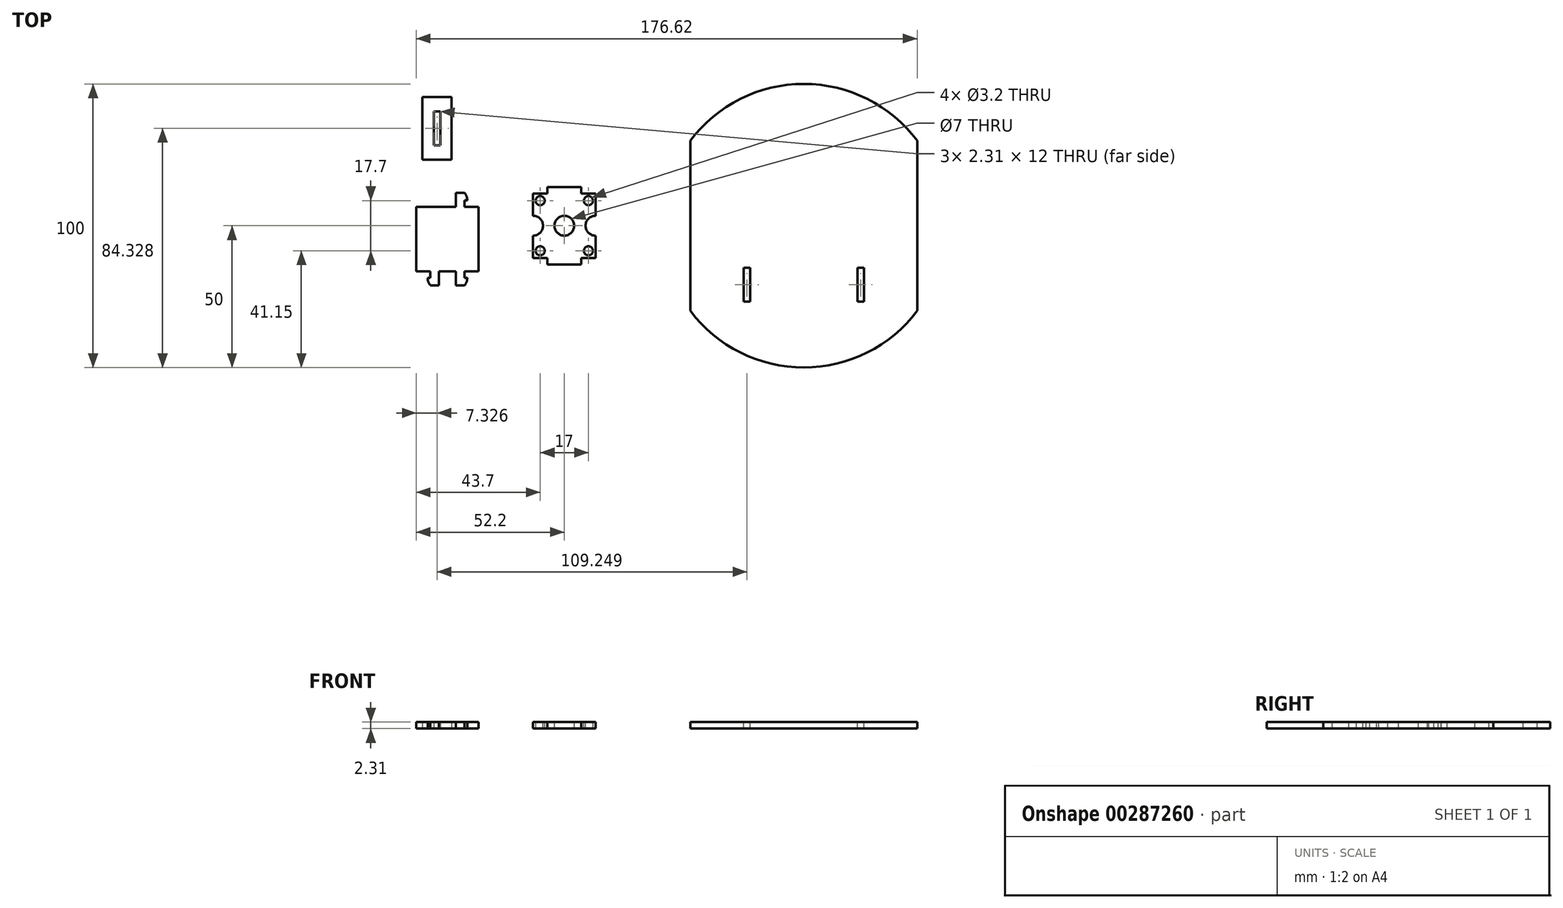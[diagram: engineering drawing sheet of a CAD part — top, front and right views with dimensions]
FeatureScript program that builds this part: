
annotation { "Feature Type Name" : "Feature", "Feature Type Description" : "" }
export const myFeature = defineFeature(function(context is Context, id is Id, definition is map)
    precondition{}
    {
        {
            var Q0;
            Q0=qCreatedBy(makeId("Top.planeOp"),FACE);
            var sketch = newSketch(context, id + "F0", { "sketchPlane" : qUnion([Q0])});
            skLineSegment(sketch, "E0.bottom", {"start": v(11, -11.35) * mm, "end": v(-11, -11.35) * mm});
            skLineSegment(sketch, "E0.top", {"start": v(11, 11.35) * mm, "end": v(-11, 11.35) * mm});
            skLineSegment(sketch, "E0.left", {"start": v(11, -11.35) * mm, "end": v(11, 11.35) * mm});
            skLineSegment(sketch, "E0.right", {"start": v(-11, -11.35) * mm, "end": v(-11, 11.35) * mm});
            skPoint(sketch, "E0.middle", {"position": v(0, 0) * mm});
            skSolve(sketch);
        }
        {
            var Q0;
            Q0=makeQuery(id+"F0.imprint","IMPRINT",FACE,{"disambiguationData":[TD([[makeQuery(id+"F0.imprint","IMPRINT",EDGE,{"derivedFrom":sQuery(id+"F0.wireOp",EDGE,"E0.bottom")}),-1.0]])]});
            extrude(context, id + "F1", {"entities" : qUnion([Q0]), "depth" : 2.31 * mm});
        }
        {
            var Q0;
            Q0=makeQuery(id+"F1.opExtrude","CAP_FACE",FACE,{"disambiguationData":[OSD([sQuery(id+"F0.wireOp",EDGE,"E0.bottom"),sQuery(id+"F0.wireOp",EDGE,"E0.top"),sQuery(id+"F0.wireOp",EDGE,"E0.left"),sQuery(id+"F0.wireOp",EDGE,"E0.right")])],"isStart":false});
            var sketch = newSketch(context, id + "F2", { "sketchPlane" : qUnion([Q0])});
            skPoint(sketch, "E1", {"position": v(-8.5, 8.85) * mm});
            skPoint(sketch, "E2.MirrorP", {"position": v(-8.5, -8.85) * mm});
            skPoint(sketch, "E3.MirrorP", {"position": v(8.5, 8.85) * mm});
            skPoint(sketch, "E4.MirrorP", {"position": v(8.5, -8.85) * mm});
            skSolve(sketch);
        }
        {
            var Q0;
            Q0=sQuery(id+"F2.wireOp",VERTEX,"E1");
            var Q1;
            Q1=sQuery(id+"F2.wireOp",VERTEX,"E3.MirrorP");
            var Q2;
            Q2=sQuery(id+"F2.wireOp",VERTEX,"E4.MirrorP");
            var Q3;
            Q3=sQuery(id+"F2.wireOp",VERTEX,"E2.MirrorP");
            var Q4;
            Q4=makeQuery(id+"F1.opExtrude","SWEPT_BODY",BODY,{"disambiguationData":[OSD([sQuery(id+"F0.wireOp",EDGE,"E0.bottom"),sQuery(id+"F0.wireOp",EDGE,"E0.top"),sQuery(id+"F0.wireOp",EDGE,"E0.left"),sQuery(id+"F0.wireOp",EDGE,"E0.right")])]});
            hole(context, id + "F3", {"style" : HoleStyle.SIMPLE, "endStyle" : HoleEndStyle.THROUGH, "holeDiameter" : 3.2 * mm, "tappedDepth" : 12 * mm, "tapClearance" : 3, "locations" : qUnion([Q0, Q1, Q2, Q3]), "scope" : qUnion([Q4])});
        }
        {
            var Q0;
            Q0=makeQuery(id+"F1.opExtrude","CAP_FACE",FACE,{"disambiguationData":[OSD([sQuery(id+"F0.wireOp",EDGE,"E0.bottom"),sQuery(id+"F0.wireOp",EDGE,"E0.top"),sQuery(id+"F0.wireOp",EDGE,"E0.left"),sQuery(id+"F0.wireOp",EDGE,"E0.right")])],"isStart":false});
            var sketch = newSketch(context, id + "F4", { "sketchPlane" : qUnion([Q0])});
            skLineSegment(sketch, "E5.bottom", {"start": v(6, -13.66) * mm, "end": v(-6, -13.66) * mm});
            skLineSegment(sketch, "E5.top", {"start": v(6, 13.66) * mm, "end": v(-6, 13.66) * mm});
            skLineSegment(sketch, "E5.left", {"start": v(6, -13.66) * mm, "end": v(6, 13.66) * mm});
            skLineSegment(sketch, "E5.right", {"start": v(-6, -13.66) * mm, "end": v(-6, 13.66) * mm});
            skPoint(sketch, "E5.middle", {"position": v(0, 0) * mm});
            skSolve(sketch);
        }
        {
            var Q0;
            {var subQ0=sQuery(id+"F4.wireOp",EDGE,"E5.top");Q0=makeQuery(id+"F4.imprint","IMPRINT",FACE,{"disambiguationData":[TD([[makeQuery(id+"F4.imprint","IMPRINT",EDGE,{"derivedFrom":subQ0}),1.0]])]});}
            var Q1;
            {var subQ0=sQuery(id+"F4.wireOp",EDGE,"E5.bottom");Q1=makeQuery(id+"F4.imprint","IMPRINT",FACE,{"disambiguationData":[TD([[makeQuery(id+"F4.imprint","IMPRINT",EDGE,{"derivedFrom":subQ0}),-1.0]])]});}
            extrude(context, id + "F5", {"entities" : qUnion([Q0, Q1]), "oppositeDirection" : true, "depth" : 2.31 * mm});
        }
        {
            var Q0;
            Q0=makeQuery(id+"F1.opExtrude","SWEPT_BODY",BODY,{"disambiguationData":[OSD([sQuery(id+"F0.wireOp",EDGE,"E0.bottom"),sQuery(id+"F0.wireOp",EDGE,"E0.top"),sQuery(id+"F0.wireOp",EDGE,"E0.left"),sQuery(id+"F0.wireOp",EDGE,"E0.right")])]});
            var Q1;
            Q1=makeQuery(id+"F5.opExtrude","SWEPT_BODY",BODY,{"disambiguationData":[OSD([sQuery(id+"F0.wireOp",EDGE,"E0.top"),sQuery(id+"F4.wireOp",EDGE,"E5.top"),sQuery(id+"F4.wireOp",EDGE,"E5.left"),sQuery(id+"F4.wireOp",EDGE,"E5.right")])]});
            var Q2;
            Q2=makeQuery(id+"F5.opExtrude","SWEPT_BODY",BODY,{"disambiguationData":[OSD([sQuery(id+"F0.wireOp",EDGE,"E0.bottom"),sQuery(id+"F4.wireOp",EDGE,"E5.bottom"),sQuery(id+"F4.wireOp",EDGE,"E5.left"),sQuery(id+"F4.wireOp",EDGE,"E5.right")])]});
            booleanBodies(context, id + "F6", {"operationType" : BooleanOperationType.UNION, "tools" : qUnion([Q0, Q1, Q2])});
        }
        {
            var Q0;
            {var subQ0=sQuery(id+"F4.wireOp",EDGE,"E5.right");var subQ1=sQuery(id+"F4.wireOp",EDGE,"E5.left");var subQ2=sQuery(id+"F0.wireOp",EDGE,"E0.top");var subQ3=sQuery(id+"F0.wireOp",EDGE,"E0.bottom");Q0=makeQuery(id+"F6.opBoolean","MERGE",FACE,{"derivedFrom":[makeQuery(id+"F1.opExtrude","CAP_FACE",FACE,{"disambiguationData":[OSD([subQ3,subQ2,sQuery(id+"F0.wireOp",EDGE,"E0.left"),sQuery(id+"F0.wireOp",EDGE,"E0.right")])],"isStart":false}),makeQuery(id+"F5.opExtrude","CAP_FACE",FACE,{"disambiguationData":[OSD([subQ3,sQuery(id+"F4.wireOp",EDGE,"E5.bottom"),subQ1,subQ0])],"isStart":true}),makeQuery(id+"F5.opExtrude","CAP_FACE",FACE,{"disambiguationData":[OSD([subQ2,sQuery(id+"F4.wireOp",EDGE,"E5.top"),subQ1,subQ0])],"isStart":true})]});}
            var sketch = newSketch(context, id + "F7", { "sketchPlane" : qUnion([Q0])});
            skPoint(sketch, "E6", {"position": v(-11, 0) * mm});
            skPoint(sketch, "E7", {"position": v(11, 0) * mm});
            skPoint(sketch, "E8", {"position": v(0, 0) * mm});
            skSolve(sketch);
        }
        {
            var Q0;
            Q0=sQuery(id+"F7.wireOp",VERTEX,"E6");
            var Q1;
            Q1=sQuery(id+"F7.wireOp",VERTEX,"E7");
            var Q2;
            Q2=sQuery(id+"F7.wireOp",VERTEX,"E8");
            var Q3;
            Q3=makeQuery(id+"F1.opExtrude","SWEPT_BODY",BODY,{"disambiguationData":[OSD([sQuery(id+"F0.wireOp",EDGE,"E0.bottom"),sQuery(id+"F0.wireOp",EDGE,"E0.top"),sQuery(id+"F0.wireOp",EDGE,"E0.left"),sQuery(id+"F0.wireOp",EDGE,"E0.right")])]});
            hole(context, id + "F8", {"style" : HoleStyle.SIMPLE, "endStyle" : HoleEndStyle.THROUGH, "holeDiameter" : 7 * mm, "tappedDepth" : 12 * mm, "tapClearance" : 3, "locations" : qUnion([Q0, Q1, Q2]), "scope" : qUnion([Q3])});
        }
        {
            var Q0;
            Q0=qCreatedBy(makeId("Top.planeOp"),FACE);
            var sketch = newSketch(context, id + "F9", { "sketchPlane" : qUnion([Q0])});
            skCircle(sketch, "E9", {"center": v(84.42, 0) * mm, "radius": 50 * mm});
            skLineSegment(sketch, "E10.bottom", {"start": v(44.42, 50) * mm, "end": v(124.42, 50) * mm});
            skLineSegment(sketch, "E10.top", {"start": v(44.42, -50) * mm, "end": v(124.42, -50) * mm});
            skLineSegment(sketch, "E10.left", {"start": v(44.42, 50) * mm, "end": v(44.42, -50) * mm});
            skLineSegment(sketch, "E10.right", {"start": v(124.42, 50) * mm, "end": v(124.42, -50) * mm});
            skLineSegment(sketch, "E11", {"start": v(84.42, 50) * mm, "end": v(84.42, 0) * mm});
            skPoint(sketch, "E12", {"position": v(84.42, 50) * mm});
            skSolve(sketch);
        }
        {
            var Q0;
            Q0=makeQuery(id+"F9.imprint","IMPRINT",FACE,{"disambiguationData":[TD([[makeQuery(id+"F9.imprint","IMPRINT",EDGE,{"derivedFrom":sQuery(id+"F9.wireOp",EDGE,"n7RTJ1XV-eWxd-Xe3c-fP3V-9vTSdCg1LdaS.bottom")}),-1.0]])]});
            var Q1;
            {var subQ0=sQuery(id+"F9.wireOp",EDGE,"E9");var subQ7=makeQuery(id+"F9.imprint","INTERSECT",VERTEX,{"derivedFrom":[subQ0,sQuery(id+"F9.wireOp",EDGE,"E10.bottom")]});Q1=makeQuery(id+"F9.imprint","IMPRINT",FACE,{"disambiguationData":[TD([[makeQuery(id+"F9.imprint","IMPRINT",EDGE,{"disambiguationData":[TD([[subQ7,1.0]])],"derivedFrom":subQ0}),1.0]])]});}
            extrude(context, id + "F10", {"entities" : qUnion([Q0, Q1]), "depth" : 2.31 * mm});
        }
        {
            var Q0;
            Q0=makeQuery(id+"F10.opExtrude","CAP_FACE",FACE,{"disambiguationData":[OSD([sQuery(id+"F9.wireOp",EDGE,"E9"),sQuery(id+"F9.wireOp",EDGE,"E10.left"),sQuery(id+"F9.wireOp",EDGE,"E10.right")])],"isStart":false});
            var sketch = newSketch(context, id + "F11", { "sketchPlane" : qUnion([Q0])});
            skLineSegment(sketch, "E13.bottom", {"start": v(63.22, -14.83) * mm, "end": v(65.53, -14.83) * mm});
            skLineSegment(sketch, "E13.top", {"start": v(63.22, -26.83) * mm, "end": v(65.53, -26.83) * mm});
            skLineSegment(sketch, "E13.left", {"start": v(63.22, -14.83) * mm, "end": v(63.22, -26.83) * mm});
            skLineSegment(sketch, "E13.right", {"start": v(65.53, -14.83) * mm, "end": v(65.53, -26.83) * mm});
            skLineSegment(sketch, "E14", {"start": v(84.42, 50) * mm, "end": v(84.42, -50) * mm});
            skLineSegment(sketch, "E15.MirrorCS", {"start": v(105.62, -14.83) * mm, "end": v(103.3, -14.83) * mm});
            skLineSegment(sketch, "E16.MirrorCS", {"start": v(105.62, -26.83) * mm, "end": v(103.3, -26.83) * mm});
            skLineSegment(sketch, "E17.MirrorCS", {"start": v(103.3, -14.83) * mm, "end": v(103.3, -26.83) * mm});
            skLineSegment(sketch, "E18.MirrorCS", {"start": v(105.62, -14.83) * mm, "end": v(105.62, -26.83) * mm});
            skSolve(sketch);
        }
        {
            var Q0;
            Q0=makeQuery(id+"F11.imprint","IMPRINT",FACE,{"disambiguationData":[TD([[makeQuery(id+"F11.imprint","IMPRINT",EDGE,{"derivedFrom":sQuery(id+"F11.wireOp",EDGE,"E13.bottom")}),-1.0]])]});
            var Q1;
            Q1=makeQuery(id+"F11.imprint","IMPRINT",FACE,{"disambiguationData":[TD([[makeQuery(id+"F11.imprint","IMPRINT",EDGE,{"derivedFrom":sQuery(id+"F11.wireOp",EDGE,"E15.MirrorCS")}),1.0]])]});
            extrude(context, id + "F12", {"entities" : qUnion([Q0, Q1]), "operationType" : NewBodyOperationType.REMOVE, "endBound" : BoundingType.THROUGH_ALL, "oppositeDirection" : true, "depth" : 2.2 * mm});
        }
        {
            var Q0;
            Q0=qCreatedBy(makeId("Top.planeOp"),FACE);
            var sketch = newSketch(context, id + "F13", { "sketchPlane" : qUnion([Q0])});
            skLineSegment(sketch, "E19.bottom", {"start": v(-52.2, 6.6) * mm, "end": v(-30.2, 6.6) * mm});
            skLineSegment(sketch, "E19.top", {"start": v(-52.2, -16.1) * mm, "end": v(-30.2, -16.1) * mm});
            skLineSegment(sketch, "E19.left", {"start": v(-52.2, 6.6) * mm, "end": v(-52.2, -16.1) * mm});
            skLineSegment(sketch, "E19.right", {"start": v(-30.2, 6.6) * mm, "end": v(-30.2, -16.1) * mm});
            skLineSegment(sketch, "E20", {"start": v(-41.2, -16.1) * mm, "end": v(-41.2, 6.6) * mm});
            skLineSegment(sketch, "E21", {"start": v(-47.2, 8.91) * mm, "end": v(-47.2, -4.75) * mm});
            skLineSegment(sketch, "E22", {"start": v(-44.2, 8.91) * mm, "end": v(-44.2, -4.75) * mm});
            skCircle(sketch, "E23", {"center": v(-42.22, 33.17) * mm, "radius": 4 * mm});
            skLineSegment(sketch, "E24", {"start": v(-42.22, 33.17) * mm, "end": v(-42.22, 37.17) * mm});
            skLineSegment(sketch, "E25", {"start": v(-42.22, 33.17) * mm, "end": v(-46.22, 33.17) * mm});
            skArc(sketch, "E26", {"start": v(-48.2, 8.91) * mm, "mid": v(-47.94, 10.33) * mm, "end": v(-47.2, 11.56) * mm});
            skLineSegment(sketch, "E27", {"start": v(-47.2, 8.91) * mm, "end": v(-48.2, 8.91) * mm});
            skLineSegment(sketch, "E28", {"start": v(-47.2, 11.56) * mm, "end": v(-44.2, 11.56) * mm});
            skLineSegment(sketch, "E29", {"start": v(-44.2, 11.56) * mm, "end": v(-44.2, 8.91) * mm});
            skLineSegment(sketch, "E30", {"start": v(-52.2, -4.75) * mm, "end": v(-30.2, -4.75) * mm});
            skLineSegment(sketch, "E31.MirrorCS", {"start": v(-47.2, -18.41) * mm, "end": v(-48.2, -18.41) * mm});
            skLineSegment(sketch, "E32.MirrorCS", {"start": v(-44.2, -21.06) * mm, "end": v(-44.2, -18.41) * mm});
            skLineSegment(sketch, "E33.MirrorCS", {"start": v(-47.2, -18.41) * mm, "end": v(-47.2, -4.75) * mm});
            skLineSegment(sketch, "E34.MirrorCS", {"start": v(-44.2, -18.41) * mm, "end": v(-44.2, -4.75) * mm});
            skLineSegment(sketch, "E35.MirrorCS", {"start": v(-47.2, -21.06) * mm, "end": v(-44.2, -21.06) * mm});
            skArc(sketch, "E36.MirrorCS", {"start": v(-48.2, -18.41) * mm, "mid": v(-47.94, -19.83) * mm, "end": v(-47.2, -21.06) * mm});
            skLineSegment(sketch, "E37.MirrorCS", {"start": v(-35.2, 8.91) * mm, "end": v(-34.2, 8.91) * mm});
            skLineSegment(sketch, "E38.MirrorCS", {"start": v(-35.2, -18.41) * mm, "end": v(-34.2, -18.41) * mm});
            skLineSegment(sketch, "E39.MirrorCS", {"start": v(-35.2, 8.91) * mm, "end": v(-35.2, -4.75) * mm});
            skArc(sketch, "E40.MirrorCS", {"start": v(-34.2, -18.41) * mm, "mid": v(-34.46, -19.83) * mm, "end": v(-35.2, -21.06) * mm});
            skLineSegment(sketch, "E41.MirrorCS", {"start": v(-35.2, -18.41) * mm, "end": v(-35.2, -4.75) * mm});
            skLineSegment(sketch, "E42.MirrorCS", {"start": v(-38.2, 8.91) * mm, "end": v(-38.2, -4.75) * mm});
            skLineSegment(sketch, "E43.MirrorCS", {"start": v(-38.2, -21.06) * mm, "end": v(-38.2, -18.41) * mm});
            skLineSegment(sketch, "E44.MirrorCS", {"start": v(-35.2, 11.56) * mm, "end": v(-38.2, 11.56) * mm});
            skArc(sketch, "E45.MirrorCS", {"start": v(-34.2, 8.91) * mm, "mid": v(-34.46, 10.33) * mm, "end": v(-35.2, 11.56) * mm});
            skLineSegment(sketch, "E46.MirrorCS", {"start": v(-38.2, 11.56) * mm, "end": v(-38.2, 8.91) * mm});
            skLineSegment(sketch, "E47.MirrorCS", {"start": v(-38.2, -18.41) * mm, "end": v(-38.2, -4.75) * mm});
            skLineSegment(sketch, "E48.MirrorCS", {"start": v(-35.2, -21.06) * mm, "end": v(-38.2, -21.06) * mm});
            skSolve(sketch);
        }
        {
            var Q0;
            {var subQ0=sQuery(id+"F13.wireOp",EDGE,"E19.left");var subQ1=sQuery(id+"F13.wireOp",EDGE,"E19.bottom");var subQ2=makeQuery(id+"F13.imprint","INTERSECT",VERTEX,{"derivedFrom":[subQ1,subQ0]});Q0=makeQuery(id+"F13.imprint","IMPRINT",FACE,{"disambiguationData":[TD([[makeQuery(id+"F13.imprint","IMPRINT",EDGE,{"disambiguationData":[TD([[subQ2,-1.0]])],"derivedFrom":subQ1}),-1.0]])]});}
            var Q1;
            {var subQ0=sQuery(id+"F13.wireOp",EDGE,"E21");var subQ1=sQuery(id+"F13.wireOp",EDGE,"E19.bottom");var subQ2=makeQuery(id+"F13.imprint","INTERSECT",VERTEX,{"derivedFrom":[subQ1,subQ0]});Q1=makeQuery(id+"F13.imprint","IMPRINT",FACE,{"disambiguationData":[TD([[makeQuery(id+"F13.imprint","IMPRINT",EDGE,{"disambiguationData":[TD([[subQ2,-1.0]])],"derivedFrom":subQ1}),-1.0]])]});}
            var Q2;
            {var subQ0=sQuery(id+"F13.wireOp",EDGE,"E20");var subQ1=sQuery(id+"F13.wireOp",EDGE,"E19.bottom");var subQ2=makeQuery(id+"F13.imprint","INTERSECT",VERTEX,{"derivedFrom":[subQ1,subQ0]});Q2=makeQuery(id+"F13.imprint","IMPRINT",FACE,{"disambiguationData":[TD([[makeQuery(id+"F13.imprint","IMPRINT",EDGE,{"disambiguationData":[TD([[subQ2,-1.0]])],"derivedFrom":subQ1}),-1.0]])]});}
            var Q3;
            {var subQ0=sQuery(id+"F13.wireOp",EDGE,"E20");var subQ1=sQuery(id+"F13.wireOp",EDGE,"E19.top");var subQ2=makeQuery(id+"F13.imprint","INTERSECT",VERTEX,{"derivedFrom":[subQ1,subQ0]});Q3=makeQuery(id+"F13.imprint","IMPRINT",FACE,{"disambiguationData":[TD([[makeQuery(id+"F13.imprint","IMPRINT",EDGE,{"disambiguationData":[TD([[subQ2,-1.0]])],"derivedFrom":subQ1}),1.0]])]});}
            var Q4;
            {var subQ0=sQuery(id+"F13.wireOp",EDGE,"E19.left");var subQ1=sQuery(id+"F13.wireOp",EDGE,"E19.top");var subQ2=makeQuery(id+"F13.imprint","INTERSECT",VERTEX,{"derivedFrom":[subQ1,subQ0]});Q4=makeQuery(id+"F13.imprint","IMPRINT",FACE,{"disambiguationData":[TD([[makeQuery(id+"F13.imprint","IMPRINT",EDGE,{"disambiguationData":[TD([[subQ2,-1.0]])],"derivedFrom":subQ1}),1.0]])]});}
            var Q5;
            {var subQ0=sQuery(id+"F13.wireOp",EDGE,"E19.right");var subQ1=sQuery(id+"F13.wireOp",EDGE,"E19.top");var subQ2=makeQuery(id+"F13.imprint","INTERSECT",VERTEX,{"derivedFrom":[subQ1,subQ0]});Q5=makeQuery(id+"F13.imprint","IMPRINT",FACE,{"disambiguationData":[TD([[makeQuery(id+"F13.imprint","IMPRINT",EDGE,{"disambiguationData":[TD([[subQ2,1.0]])],"derivedFrom":subQ1}),1.0]])]});}
            var Q6;
            {var subQ0=sQuery(id+"F13.wireOp",EDGE,"E19.right");var subQ1=sQuery(id+"F13.wireOp",EDGE,"E19.bottom");var subQ2=makeQuery(id+"F13.imprint","INTERSECT",VERTEX,{"derivedFrom":[subQ1,subQ0]});Q6=makeQuery(id+"F13.imprint","IMPRINT",FACE,{"disambiguationData":[TD([[makeQuery(id+"F13.imprint","IMPRINT",EDGE,{"disambiguationData":[TD([[subQ2,1.0]])],"derivedFrom":subQ1}),-1.0]])]});}
            var Q7;
            {var subQ1=sQuery(id+"F13.wireOp",EDGE,"E38.MirrorCS");Q7=makeQuery(id+"F13.imprint","IMPRINT",FACE,{"disambiguationData":[TD([[makeQuery(id+"F13.imprint","IMPRINT",EDGE,{"derivedFrom":subQ1}),-1.0]])]});}
            var Q8;
            {var subQ0=sQuery(id+"F13.wireOp",EDGE,"E33.MirrorCS");var subQ1=sQuery(id+"F13.wireOp",EDGE,"E19.top");var subQ2=makeQuery(id+"F13.imprint","INTERSECT",VERTEX,{"derivedFrom":[subQ1,subQ0]});Q8=makeQuery(id+"F13.imprint","IMPRINT",FACE,{"disambiguationData":[TD([[makeQuery(id+"F13.imprint","IMPRINT",EDGE,{"disambiguationData":[TD([[subQ2,-1.0]])],"derivedFrom":subQ1}),1.0]])]});}
            var Q9;
            {var subQ0=sQuery(id+"F13.wireOp",EDGE,"E42.MirrorCS");var subQ1=sQuery(id+"F13.wireOp",EDGE,"E19.bottom");var subQ2=makeQuery(id+"F13.imprint","INTERSECT",VERTEX,{"derivedFrom":[subQ1,subQ0]});Q9=makeQuery(id+"F13.imprint","IMPRINT",FACE,{"disambiguationData":[TD([[makeQuery(id+"F13.imprint","IMPRINT",EDGE,{"disambiguationData":[TD([[subQ2,-1.0]])],"derivedFrom":subQ1}),-1.0]])]});}
            var Q10;
            {var subQ0=sQuery(id+"F13.wireOp",EDGE,"E20");var subQ1=sQuery(id+"F13.wireOp",EDGE,"E19.bottom");var subQ2=makeQuery(id+"F13.imprint","INTERSECT",VERTEX,{"derivedFrom":[subQ1,subQ0]});Q10=makeQuery(id+"F13.imprint","IMPRINT",FACE,{"disambiguationData":[TD([[makeQuery(id+"F13.imprint","IMPRINT",EDGE,{"disambiguationData":[TD([[subQ2,1.0]])],"derivedFrom":subQ1}),-1.0]])]});}
            var Q11;
            {var subQ0=sQuery(id+"F13.wireOp",EDGE,"E20");var subQ1=sQuery(id+"F13.wireOp",EDGE,"E19.top");var subQ2=makeQuery(id+"F13.imprint","INTERSECT",VERTEX,{"derivedFrom":[subQ1,subQ0]});Q11=makeQuery(id+"F13.imprint","IMPRINT",FACE,{"disambiguationData":[TD([[makeQuery(id+"F13.imprint","IMPRINT",EDGE,{"disambiguationData":[TD([[subQ2,1.0]])],"derivedFrom":subQ1}),1.0]])]});}
            var Q12;
            {var subQ0=sQuery(id+"F13.wireOp",EDGE,"E47.MirrorCS");var subQ1=sQuery(id+"F13.wireOp",EDGE,"E19.top");var subQ2=makeQuery(id+"F13.imprint","INTERSECT",VERTEX,{"derivedFrom":[subQ1,subQ0]});Q12=makeQuery(id+"F13.imprint","IMPRINT",FACE,{"disambiguationData":[TD([[makeQuery(id+"F13.imprint","IMPRINT",EDGE,{"disambiguationData":[TD([[subQ2,-1.0]])],"derivedFrom":subQ1}),1.0]])]});}
            var Q13;
            Q13=makeQuery(id+"F13.imprint","IMPRINT",FACE,{"disambiguationData":[TD([[makeQuery(id+"F13.imprint","IMPRINT",EDGE,{"derivedFrom":sQuery(id+"F13.wireOp",EDGE,"E26")}),-1.0]])]});
            var Q14;
            {var subQ5=sQuery(id+"F13.wireOp",EDGE,"E37.MirrorCS");Q14=makeQuery(id+"F13.imprint","IMPRINT",FACE,{"disambiguationData":[TD([[makeQuery(id+"F13.imprint","IMPRINT",EDGE,{"derivedFrom":subQ5}),1.0]])]});}
            var Q15;
            {var subQ1=sQuery(id+"F13.wireOp",EDGE,"E31.MirrorCS");Q15=makeQuery(id+"F13.imprint","IMPRINT",FACE,{"disambiguationData":[TD([[makeQuery(id+"F13.imprint","IMPRINT",EDGE,{"derivedFrom":subQ1}),1.0]])]});}
            extrude(context, id + "F14", {"entities" : qUnion([Q0, Q1, Q2, Q3, Q4, Q5, Q6, Q7, Q8, Q9, Q10, Q11, Q12, Q13, Q14, Q15]), "depth" : 2.31 * mm});
        }
        {
            var Q0;
            Q0=qCreatedBy(makeId("Top.planeOp"),FACE);
            var sketch = newSketch(context, id + "F15", { "sketchPlane" : qUnion([Q0])});
            skLineSegment(sketch, "E49.bottom", {"start": v(-50.03, 45.33) * mm, "end": v(-39.72, 45.33) * mm});
            skLineSegment(sketch, "E49.top", {"start": v(-50.03, 23.33) * mm, "end": v(-39.72, 23.33) * mm});
            skLineSegment(sketch, "E49.left", {"start": v(-50.03, 45.33) * mm, "end": v(-50.03, 23.33) * mm});
            skLineSegment(sketch, "E49.right", {"start": v(-39.72, 45.33) * mm, "end": v(-39.72, 23.33) * mm});
            skLineSegment(sketch, "E50.bottom", {"start": v(-46.03, 28.33) * mm, "end": v(-43.72, 28.33) * mm});
            skLineSegment(sketch, "E50.top", {"start": v(-46.03, 40.33) * mm, "end": v(-43.72, 40.33) * mm});
            skLineSegment(sketch, "E50.left", {"start": v(-46.03, 28.33) * mm, "end": v(-46.03, 40.33) * mm});
            skLineSegment(sketch, "E50.right", {"start": v(-43.72, 28.33) * mm, "end": v(-43.72, 40.33) * mm});
            skSolve(sketch);
        }
        {
            var Q0;
            Q0=makeQuery(id+"F15.imprint","IMPRINT",FACE,{"disambiguationData":[TD([[makeQuery(id+"F15.imprint","IMPRINT",EDGE,{"derivedFrom":sQuery(id+"F15.wireOp",EDGE,"E49.bottom")}),-1.0]])]});
            extrude(context, id + "F16", {"entities" : qUnion([Q0]), "depth" : 2.2 * mm});
        }
    });
